# Revit family: 306_5fa00cb592c2425cbabb8dbb78e47b
name_source: partatom
category: Pipe Accessories
units: mm (PartAtom-declared; Revit-internal decimal feet)

## family parameters
Always vertical = Yes
Cut with Voids When Loaded = No
Part Type = Valve - Breaks Into
Round Connector Dimension = Use Diameter
Shared = No
Work Plane-Based = No

## types (1)
- VTA351 35-60°C RP3/4 -1,6
    A = 30 mm  [stored 0.0984252 ft]
    A__ve = -30 mm  [stored -0.0984252 ft]
    B = 42 mm  [stored 0.137795 ft]
    C = 52 mm  [stored 0.170604 ft]
    CAT0 = Yes
    CT2 = 21 mm
    D = 20 mm
    DT2 = 10 mm  [stored 0.0328084 ft]
    Description = Thermostatic mixing valve VTA351, PN10 internal thread
    L2D = 70 mm
    L2D_Min = 3048 mm  [stored 10 ft]
    LT2 = 35 mm  [stored 0.114829 ft]
    MC = No
    Manufacturer = ESBE
    QmdConnectorList = 301;D;302;D
    R2 = 9 mm  [stored 0.0295276 ft]
    URL = http://www.esbe.eu
    W1 = 17 mm
    W2D = 20 mm  [stored 0.0656168 ft]
    WT2 = 23 mm  [stored 0.0754593 ft]
    X1 = 2 mm  [stored 0.00656168 ft]
    X2 = 6 mm  [stored 0.019685 ft]
    X3 = 50 mm  [stored 0.164042 ft]
    X4 = 46 mm
    X6 = 8 mm  [stored 0.0262467 ft]
    Z1 = 15 mm  [stored 0.0492126 ft]
    Z1__ve = -15 mm
    Z2 = 5 mm  [stored 0.0164042 ft]
    magiPartTypeId = 306
    magiProductCode = VTA351 35-60°C RP3/4 -1,6
    magiProductFamilyId = 5fa00cb592c2425cbabb8dbb78e47b
    magiProductId = 228dbd6ccb504c25bbad79c9bf97b0

note: [stored X ft] marks values corroborated as IEEE doubles in the binary element streams (Revit-internal decimal feet)

## geometry (parser evidence)
native form markers: Sweep x1
no freeform markers — native parametric forms only
